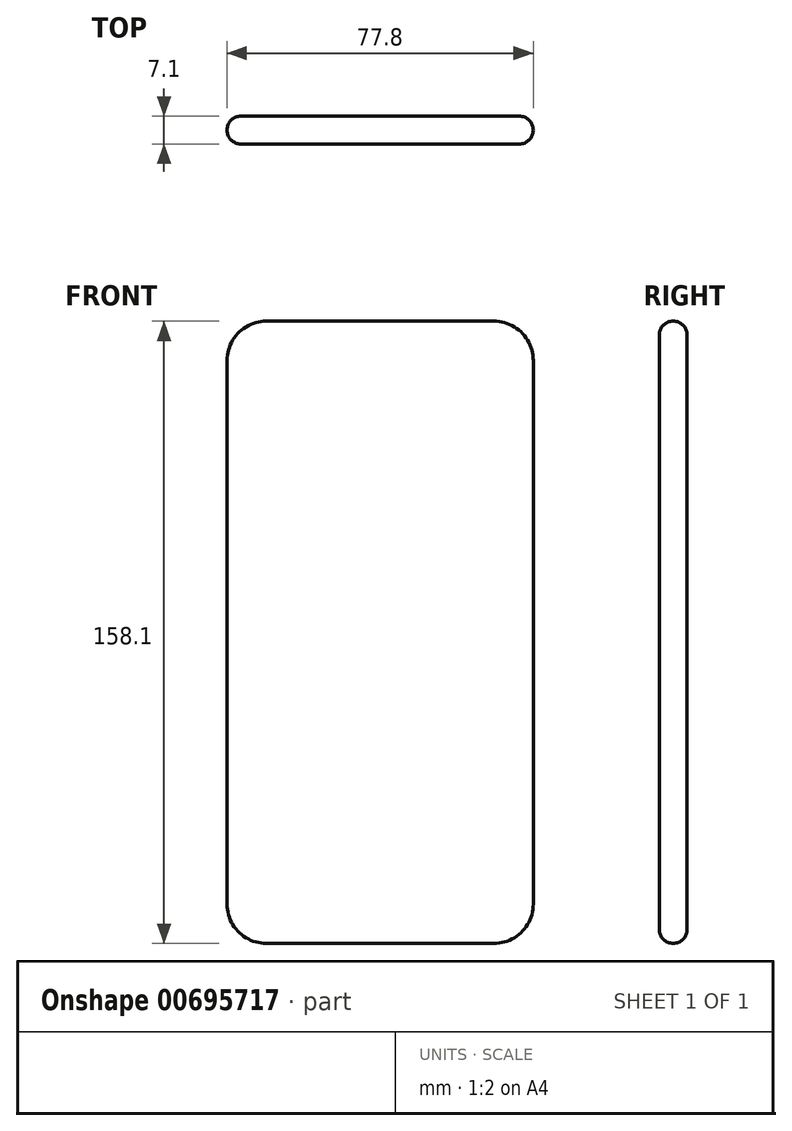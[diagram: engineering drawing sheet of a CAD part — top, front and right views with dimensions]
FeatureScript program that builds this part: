
annotation { "Feature Type Name" : "Feature", "Feature Type Description" : "" }
export const myFeature = defineFeature(function(context is Context, id is Id, definition is map)
    precondition{}
    {
        {
            var Q0;
            Q0=qCreatedBy(makeId("Front.planeOp"),FACE);
            var sketch = newSketch(context, id + "F0", { "sketchPlane" : qUnion([Q0])});
            skLineSegment(sketch, "E0", {"start": v(0, -98.15) * mm, "end": v(0, 59.95) * mm});
            skLineSegment(sketch, "E1", {"start": v(0, 59.95) * mm, "end": v(-77.8, 59.95) * mm});
            skLineSegment(sketch, "E2", {"start": v(0, -98.15) * mm, "end": v(-77.8, -98.15) * mm});
            skLineSegment(sketch, "E3", {"start": v(-77.8, 59.95) * mm, "end": v(-77.8, -98.15) * mm});
            skPoint(sketch, "E4", {"position": v(-77.8, 49.95) * mm});
            skPoint(sketch, "E5", {"position": v(-67.8, 59.95) * mm});
            skPoint(sketch, "E6", {"position": v(0, 49.95) * mm});
            skPoint(sketch, "E7", {"position": v(-10, 59.95) * mm});
            skPoint(sketch, "E8", {"position": v(0, -88.15) * mm});
            skPoint(sketch, "E9", {"position": v(-10, -98.15) * mm});
            skPoint(sketch, "E10", {"position": v(-67.8, -98.15) * mm});
            skPoint(sketch, "E11", {"position": v(-77.8, -88.15) * mm});
            skArc(sketch, "E12", {"start": v(-67.8, 59.95) * mm, "mid": v(-74.87, 57.02) * mm, "end": v(-77.8, 49.95) * mm});
            skArc(sketch, "E13", {"start": v(0, 49.95) * mm, "mid": v(-2.93, 57.02) * mm, "end": v(-10, 59.95) * mm});
            skArc(sketch, "E14", {"start": v(-10, -98.15) * mm, "mid": v(-2.93, -95.22) * mm, "end": v(0, -88.15) * mm});
            skArc(sketch, "E15", {"start": v(-77.8, -88.15) * mm, "mid": v(-74.87, -95.22) * mm, "end": v(-67.8, -98.15) * mm});
            skSolve(sketch);
        }
        {
            var Q0;
            {var subQ0=sQuery(id+"F0.wireOp",EDGE,"E12");Q0=makeQuery(id+"F0.imprint","IMPRINT",FACE,{"disambiguationData":[TD([[makeQuery(id+"F0.imprint","IMPRINT",EDGE,{"derivedFrom":subQ0}),1.0]])]});}
            extrude(context, id + "F1", {"entities" : qUnion([Q0]), "depth" : 7.1 * mm, "offsetDistance" : 25 * mm});
        }
        {
            var Q0;
            Q0=makeQuery(id+"F1.opExtrude","CAP_EDGE",EDGE,{"disambiguationData":[OSD([sQuery(id+"F0.wireOp",EDGE,"E2")])],"isStart":false});
            var Q1;
            Q1=makeQuery(id+"F1.opExtrude","CAP_EDGE",EDGE,{"disambiguationData":[OSD([sQuery(id+"F0.wireOp",EDGE,"E15")])],"isStart":false});
            var Q2;
            Q2=makeQuery(id+"F1.opExtrude","CAP_EDGE",EDGE,{"disambiguationData":[OSD([sQuery(id+"F0.wireOp",EDGE,"E3")])],"isStart":false});
            var Q3;
            Q3=makeQuery(id+"F1.opExtrude","CAP_EDGE",EDGE,{"disambiguationData":[OSD([sQuery(id+"F0.wireOp",EDGE,"E12")])],"isStart":false});
            var Q4;
            Q4=makeQuery(id+"F1.opExtrude","CAP_EDGE",EDGE,{"disambiguationData":[OSD([sQuery(id+"F0.wireOp",EDGE,"E1")])],"isStart":false});
            var Q5;
            Q5=makeQuery(id+"F1.opExtrude","CAP_EDGE",EDGE,{"disambiguationData":[OSD([sQuery(id+"F0.wireOp",EDGE,"E13")])],"isStart":false});
            var Q6;
            Q6=makeQuery(id+"F1.opExtrude","CAP_EDGE",EDGE,{"disambiguationData":[OSD([sQuery(id+"F0.wireOp",EDGE,"E0")])],"isStart":false});
            var Q7;
            Q7=makeQuery(id+"F1.opExtrude","CAP_EDGE",EDGE,{"disambiguationData":[OSD([sQuery(id+"F0.wireOp",EDGE,"E14")])],"isStart":false});
            fillet(context, id + "F2", {"entities" : qUnion([Q0, Q1, Q2, Q3, Q4, Q5, Q6, Q7]), "radius" : 3.55 * mm, "tangentPropagation" : true, "allowEdgeOverflow" : false});
        }
        {
            var Q0;
            Q0=makeQuery(id+"F1.opExtrude","CAP_EDGE",EDGE,{"disambiguationData":[OSD([sQuery(id+"F0.wireOp",EDGE,"E2")])],"isStart":true});
            var Q1;
            Q1=makeQuery(id+"F1.opExtrude","CAP_EDGE",EDGE,{"disambiguationData":[OSD([sQuery(id+"F0.wireOp",EDGE,"E14")])],"isStart":true});
            var Q2;
            Q2=makeQuery(id+"F1.opExtrude","CAP_EDGE",EDGE,{"disambiguationData":[OSD([sQuery(id+"F0.wireOp",EDGE,"E0")])],"isStart":true});
            var Q3;
            Q3=makeQuery(id+"F1.opExtrude","CAP_EDGE",EDGE,{"disambiguationData":[OSD([sQuery(id+"F0.wireOp",EDGE,"E15")])],"isStart":true});
            var Q4;
            Q4=makeQuery(id+"F1.opExtrude","CAP_EDGE",EDGE,{"disambiguationData":[OSD([sQuery(id+"F0.wireOp",EDGE,"E3")])],"isStart":true});
            var Q5;
            Q5=makeQuery(id+"F1.opExtrude","CAP_EDGE",EDGE,{"disambiguationData":[OSD([sQuery(id+"F0.wireOp",EDGE,"E12")])],"isStart":true});
            var Q6;
            Q6=makeQuery(id+"F1.opExtrude","CAP_EDGE",EDGE,{"disambiguationData":[OSD([sQuery(id+"F0.wireOp",EDGE,"E1")])],"isStart":true});
            var Q7;
            Q7=makeQuery(id+"F1.opExtrude","CAP_EDGE",EDGE,{"disambiguationData":[OSD([sQuery(id+"F0.wireOp",EDGE,"E13")])],"isStart":true});
            fillet(context, id + "F3", {"entities" : qUnion([Q0, Q1, Q2, Q3, Q4, Q5, Q6, Q7]), "radius" : 3.55 * mm, "tangentPropagation" : true, "allowEdgeOverflow" : false});
        }
    });
